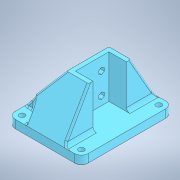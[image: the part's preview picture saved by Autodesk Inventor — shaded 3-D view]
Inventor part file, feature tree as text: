
AUTODESK INVENTOR PART (.ipt)
format: ipt  version: 2021.2 (Build 252289000, 289)  size: 439,808 bytes
history: native  units: mm
features: other x4, fillet x4, chamfer x1
ambient origin geometry x8: Origin, YZ Plane, XZ Plane, XY Plane, X Axis, Y Axis, Z Axis, Center Point
bodies: Body1 (feature_tree)
feature tree (9):
  other  "Твёрдое тело.ipt"
  fillet  "Сопряжение1"  Radius=10.0mm
  fillet  "Сопряжение2"  Radius=8.0mm
  fillet  "Сопряжение3"  Radius=4.0mm
  fillet  "Сопряжение4"  Radius=2.0mm
  chamfer  "Фаска1"  Distance=2.0mm
  other  "Фланец::Твёрдое тело.ipt"
  other  "Элемент создания тегов1"
  other  "Твердое тело1"
